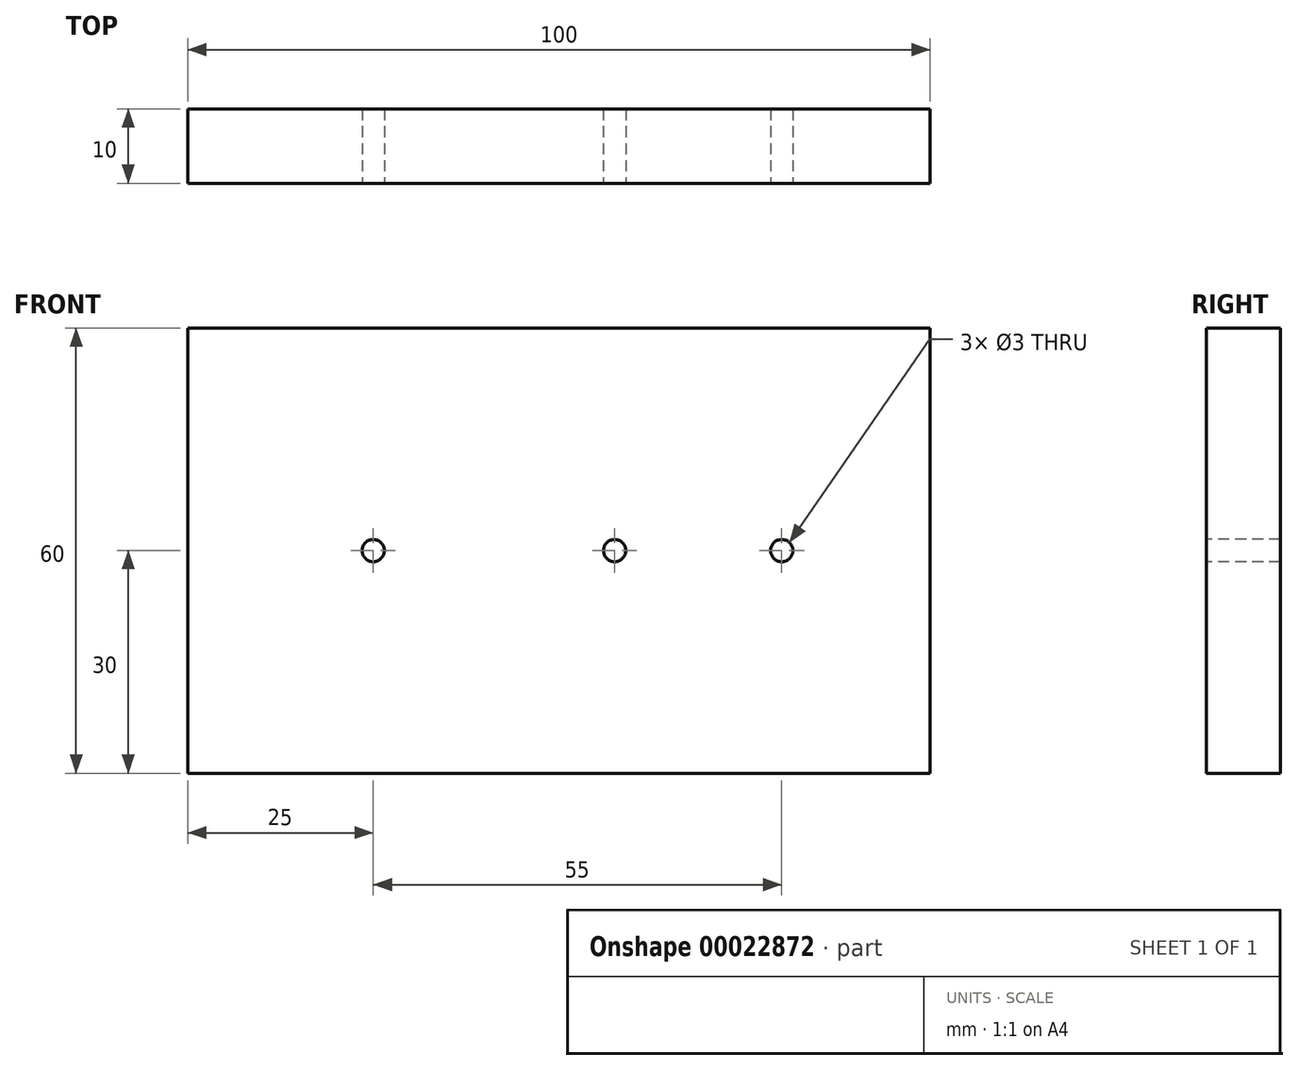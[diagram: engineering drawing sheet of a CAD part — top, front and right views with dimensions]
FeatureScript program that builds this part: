
annotation { "Feature Type Name" : "Feature", "Feature Type Description" : "" }
export const myFeature = defineFeature(function(context is Context, id is Id, definition is map)
    precondition{}
    {
        {
            var Q0;
            Q0=qCreatedBy(makeId("Front.planeOp"),FACE);
            var sketch = newSketch(context, id + "F0", { "sketchPlane" : qUnion([Q0])});
            skLineSegment(sketch, "E0", {"start": v(0, 0) * mm, "end": v(100, 0) * mm});
            skLineSegment(sketch, "E1", {"start": v(100, 0) * mm, "end": v(100, -60) * mm});
            skLineSegment(sketch, "E2", {"start": v(100, -60) * mm, "end": v(0, -60) * mm});
            skLineSegment(sketch, "E3", {"start": v(0, -60) * mm, "end": v(0, 0) * mm});
            skSolve(sketch);
        }
        {
            var Q0;
            Q0=makeQuery(id+"F0.imprint","IMPRINT",FACE,{"disambiguationData":[TD([[makeQuery(id+"F0.imprint","IMPRINT",EDGE,{"derivedFrom":sQuery(id+"F0.wireOp",EDGE,"E0")}),-1.0]])]});
            extrude(context, id + "F1", {"entities" : qUnion([Q0]), "depth" : 10 * mm});
        }
        {
            var Q0;
            Q0=makeQuery(id+"F1.opExtrude","CAP_FACE",FACE,{"disambiguationData":[OSD([sQuery(id+"F0.wireOp",EDGE,"E0"),sQuery(id+"F0.wireOp",EDGE,"E1"),sQuery(id+"F0.wireOp",EDGE,"E2"),sQuery(id+"F0.wireOp",EDGE,"E3")])],"isStart":false});
            var sketch = newSketch(context, id + "F2", { "sketchPlane" : qUnion([Q0])});
            skCircle(sketch, "E4", {"center": v(25, -30) * mm, "radius": 1.5 * mm});
            skCircle(sketch, "E5", {"center": v(57.5, -30) * mm, "radius": 1.5 * mm});
            skCircle(sketch, "E6", {"center": v(80, -30) * mm, "radius": 1.5 * mm});
            skSolve(sketch);
        }
        {
            var Q0;
            Q0=sQuery(id+"F2.wireOp",VERTEX,"E4.center");
            var Q1;
            Q1=makeQuery(id+"F1.opExtrude","SWEPT_BODY",BODY,{"disambiguationData":[OSD([sQuery(id+"F0.wireOp",EDGE,"E0"),sQuery(id+"F0.wireOp",EDGE,"E1"),sQuery(id+"F0.wireOp",EDGE,"E2"),sQuery(id+"F0.wireOp",EDGE,"E3")])]});
            hole(context, id + "F3", {"style" : HoleStyle.SIMPLE, "holeDiameter" : 3 * mm, "endStyle" : HoleEndStyle.THROUGH, "locations" : qUnion([Q0]), "scope" : qUnion([Q1])});
        }
        {
            var Q0;
            Q0=sQuery(id+"F2.wireOp",VERTEX,"E5.center");
            var Q1;
            Q1=sQuery(id+"F2.wireOp",VERTEX,"E6.center");
            var Q2;
            Q2=makeQuery(id+"F1.opExtrude","SWEPT_BODY",BODY,{"disambiguationData":[OSD([sQuery(id+"F0.wireOp",EDGE,"E0"),sQuery(id+"F0.wireOp",EDGE,"E1"),sQuery(id+"F0.wireOp",EDGE,"E2"),sQuery(id+"F0.wireOp",EDGE,"E3")])]});
            hole(context, id + "F4", {"style" : HoleStyle.SIMPLE, "holeDiameter" : 3 * mm, "endStyle" : HoleEndStyle.THROUGH, "locations" : qUnion([Q0, Q1]), "scope" : qUnion([Q2])});
        }
    });
